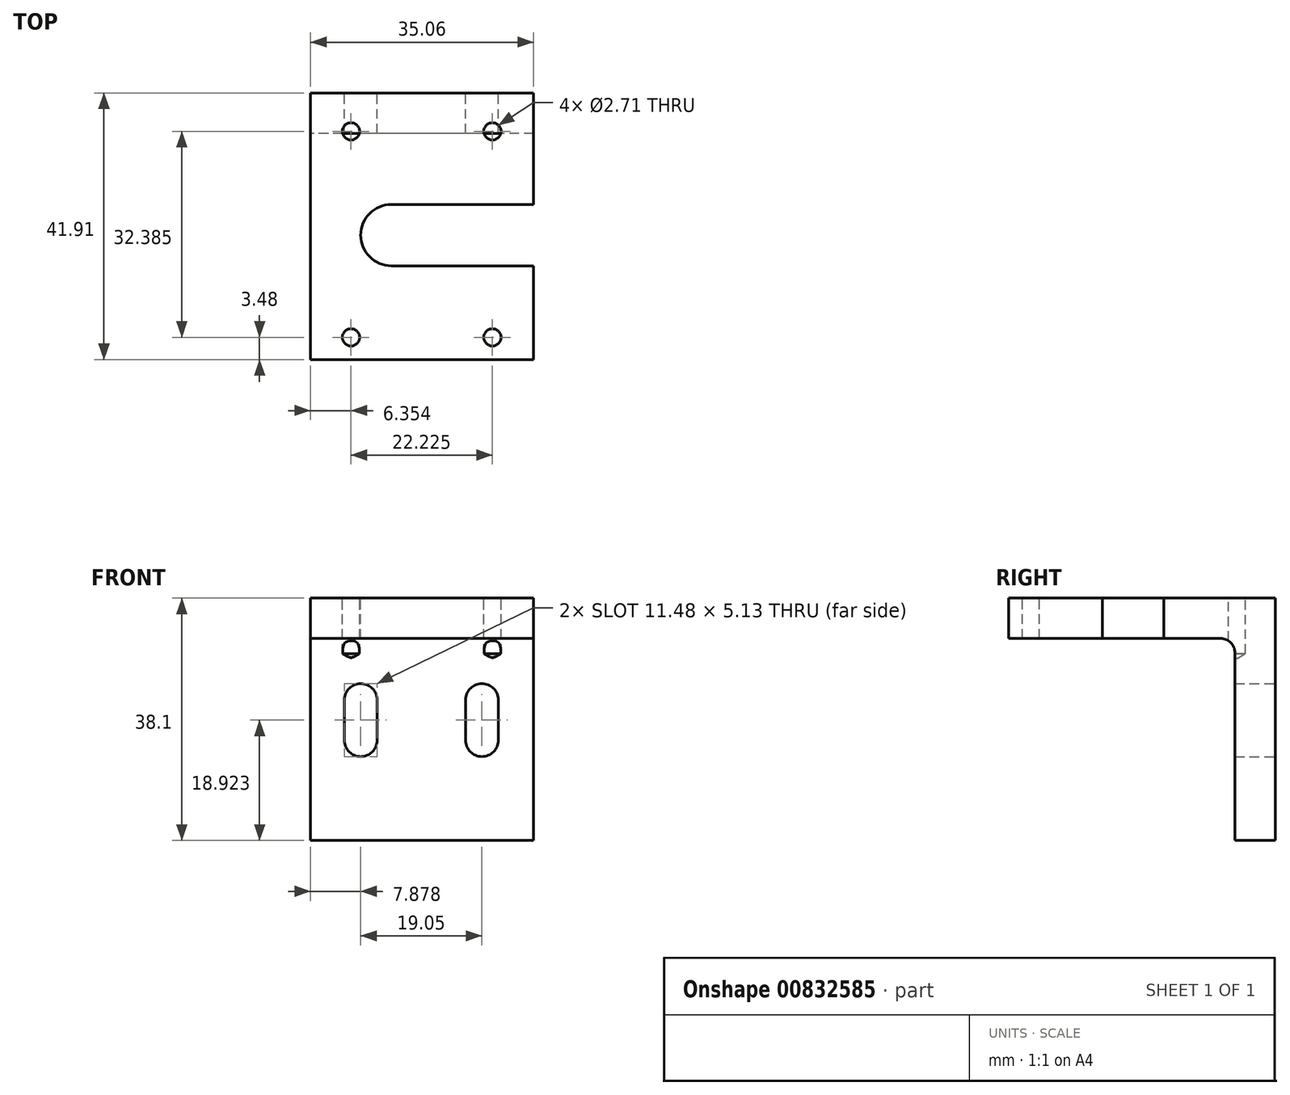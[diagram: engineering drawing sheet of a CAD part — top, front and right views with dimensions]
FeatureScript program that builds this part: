
annotation { "Feature Type Name" : "Feature", "Feature Type Description" : "" }
export const myFeature = defineFeature(function(context is Context, id is Id, definition is map)
    precondition{}
    {
        {
            var Q0;
            Q0=qCreatedBy(makeId("Right.planeOp"),FACE);
            var sketch = newSketch(context, id + "F0", { "sketchPlane" : qUnion([Q0])});
            skLineSegment(sketch, "E0", {"start": v(-41.91, 0) * mm, "end": v(0, 0) * mm});
            skLineSegment(sketch, "E1", {"start": v(0, 0) * mm, "end": v(0, -38.1) * mm});
            skLineSegment(sketch, "E2", {"start": v(0, -38.1) * mm, "end": v(-6.35, -38.1) * mm});
            skLineSegment(sketch, "E3", {"start": v(-6.35, -38.1) * mm, "end": v(-6.35, -8.64) * mm});
            skLineSegment(sketch, "E4", {"start": v(-8.64, -6.35) * mm, "end": v(-41.91, -6.35) * mm});
            skLineSegment(sketch, "E5", {"start": v(-41.91, -6.35) * mm, "end": v(-41.91, 0) * mm});
            skPoint(sketch, "E6.visualSharp", {"position": v(-6.35, -6.35) * mm});
            skArc(sketch, "E6.filletArc", {"start": v(-6.35, -8.64) * mm, "mid": v(-7.02, -7.02) * mm, "end": v(-8.64, -6.35) * mm});
            skSolve(sketch);
        }
        {
            var Q0;
            Q0 = qSketchRegion(id + "F0", true);
            extrude(context, id + "F1", {"entities" : qUnion([Q0]), "endBound" : BoundingType.SYMMETRIC, "depth" : 35.05 * mm, "offsetDistance" : 25.4 * mm});
        }
        {
            var Q0;
            Q0=makeQuery(id+"F1.opExtrude","SWEPT_FACE",FACE,{"disambiguationData":[OSD([sQuery(id+"F0.wireOp",EDGE,"E0")])]});
            var sketch = newSketch(context, id + "F2", { "sketchPlane" : qUnion([Q0])});
            skLineSegment(sketch, "E7", {"start": v(17.53, -17.53) * mm, "end": v(-4.83, -17.53) * mm});
            skLineSegment(sketch, "E8", {"start": v(17.53, -17.53) * mm, "end": v(17.53, -27.18) * mm});
            skLineSegment(sketch, "E9", {"start": v(17.53, -27.18) * mm, "end": v(-4.83, -27.18) * mm});
            skArc(sketch, "E10", {"start": v(-4.83, -17.53) * mm, "mid": v(-9.65, -22.35) * mm, "end": v(-4.83, -27.18) * mm});
            skSolve(sketch);
        }
        {
            var Q0;
            Q0 = qSketchRegion(id + "F2", true);
            extrude(context, id + "F3", {"entities" : qUnion([Q0]), "operationType" : NewBodyOperationType.REMOVE, "endBound" : BoundingType.UP_TO_NEXT, "oppositeDirection" : true, "depth" : 25.4 * mm, "offsetDistance" : 25.4 * mm});
        }
        {
            var Q0;
            Q0=makeQuery(id+"F1.opExtrude","SWEPT_FACE",FACE,{"disambiguationData":[OSD([sQuery(id+"F0.wireOp",EDGE,"E0")])]});
            var sketch = newSketch(context, id + "F4", { "sketchPlane" : qUnion([Q0])});
            skPoint(sketch, "E11", {"position": v(-11.18, -6.05) * mm});
            skPoint(sketch, "E12", {"position": v(11.05, -6.05) * mm});
            skPoint(sketch, "E13", {"position": v(-11.18, -38.43) * mm});
            skPoint(sketch, "E14", {"position": v(11.05, -38.43) * mm});
            skSolve(sketch);
        }
        {
            var Q0;
            Q0=sQuery(id+"F4.wireOp",VERTEX,"E11");
            var Q1;
            Q1=sQuery(id+"F4.wireOp",VERTEX,"E12");
            var Q2;
            Q2=sQuery(id+"F4.wireOp",VERTEX,"E13");
            var Q3;
            Q3=sQuery(id+"F4.wireOp",VERTEX,"E14");
            var Q4;
            Q4=makeQuery(id+"F1.opExtrude","SWEPT_BODY",BODY,{"disambiguationData":[OSD([sQuery(id+"F0.wireOp",EDGE,"E0"),sQuery(id+"F0.wireOp",EDGE,"E1"),sQuery(id+"F0.wireOp",EDGE,"E2"),sQuery(id+"F0.wireOp",EDGE,"E3"),sQuery(id+"F0.wireOp",EDGE,"E4"),sQuery(id+"F0.wireOp",EDGE,"E5"),sQuery(id+"F0.wireOp",EDGE,"E6.filletArc")])]});
            hole(context, id + "F5", {"style" : HoleStyle.SIMPLE, "endStyle" : HoleEndStyle.BLIND, "standardTappedOrClearance" : lookupTablePath({ "standard" : "ANSI", "engagement" : "75%", "pitch" : "32 tpi", "size" : "#6", "type" : "Tapped" }), "standardBlindInLast" : lookupTablePath({ "standard" : "ANSI", "engagement" : "75%", "pitch" : "32 tpi", "size" : "#6", "type" : "Tapped" }), "holeDiameter" : 2.7 * mm, "majorDiameter" : 3.5 * mm, "showTappedDepth" : true, "holeDepth" : 8.73 * mm, "tappedDepth" : 6.35 * mm, "tapClearance" : 3, "locations" : qUnion([Q0, Q1, Q2, Q3]), "scope" : qUnion([Q4])});
        }
        {
            var Q0;
            Q0=makeQuery(id+"F1.opExtrude","SWEPT_FACE",FACE,{"disambiguationData":[OSD([sQuery(id+"F0.wireOp",EDGE,"E1")])]});
            var sketch = newSketch(context, id + "F6", { "sketchPlane" : qUnion([Q0])});
            skLineSegment(sketch, "E15.left", {"start": v(12.22, -16) * mm, "end": v(12.22, -22.35) * mm});
            skLineSegment(sketch, "E15.right", {"start": v(7.09, -16) * mm, "end": v(7.09, -22.35) * mm});
            skLineSegment(sketch, "E16.left", {"start": v(-6.83, -16) * mm, "end": v(-6.83, -22.35) * mm});
            skLineSegment(sketch, "E16.right", {"start": v(-11.96, -16) * mm, "end": v(-11.96, -22.35) * mm});
            skArc(sketch, "E17", {"start": v(12.22, -16) * mm, "mid": v(9.65, -13.44) * mm, "end": v(7.09, -16) * mm});
            skArc(sketch, "E18", {"start": v(7.09, -22.35) * mm, "mid": v(9.65, -24.92) * mm, "end": v(12.22, -22.35) * mm});
            skArc(sketch, "E19", {"start": v(-6.83, -16) * mm, "mid": v(-9.4, -13.44) * mm, "end": v(-11.96, -16) * mm});
            skArc(sketch, "E20", {"start": v(-11.96, -22.35) * mm, "mid": v(-9.4, -24.92) * mm, "end": v(-6.83, -22.35) * mm});
            skSolve(sketch);
        }
        {
            var Q0;
            Q0 = qSketchRegion(id + "F6", true);
            extrude(context, id + "F7", {"entities" : qUnion([Q0]), "operationType" : NewBodyOperationType.REMOVE, "endBound" : BoundingType.UP_TO_NEXT, "oppositeDirection" : true, "depth" : 25.4 * mm, "offsetDistance" : 25.4 * mm});
        }
    });
